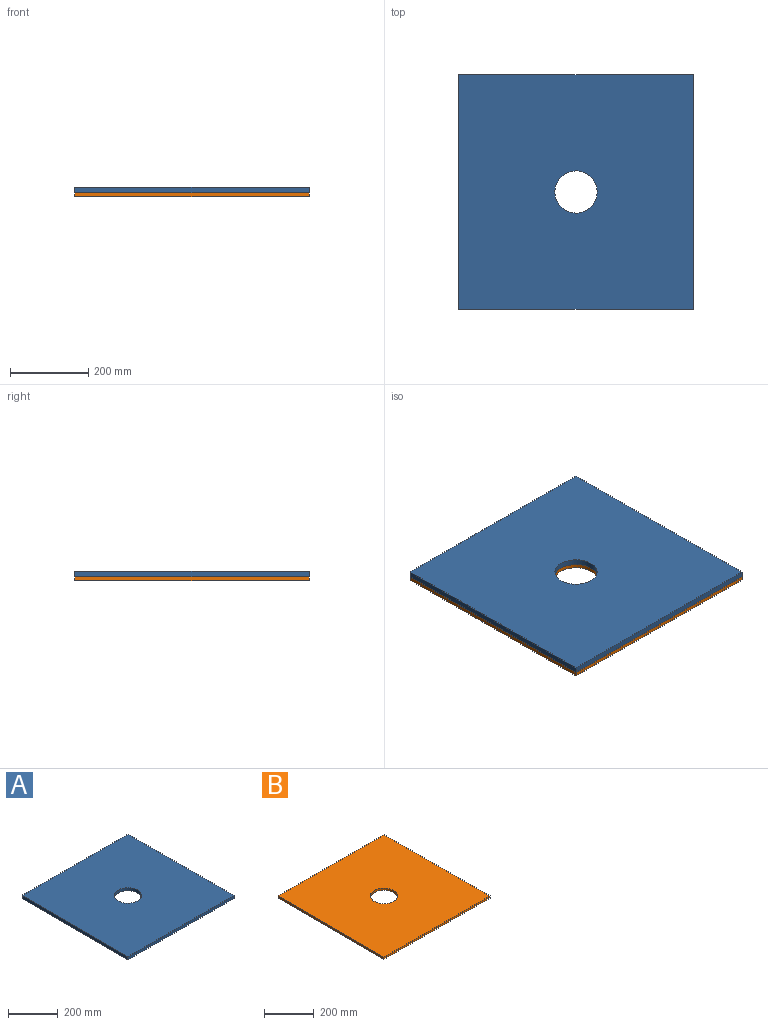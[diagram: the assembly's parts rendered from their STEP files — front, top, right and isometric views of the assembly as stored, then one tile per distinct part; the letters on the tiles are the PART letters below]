
ASSEMBLY  parts=2 mates=1
PART A: 7 faces, bbox 600x600x15 mm
  f0: plane 600x15mm, normal (-1,0,0), area 9000mm2, adj f1,f4,f5,f6
  f1: plane 600x15mm, normal (0,-1,0), area 9000mm2, adj f0,f2,f5,f6
  f2: plane 600x15mm, normal (1,0,0), area 9000mm2, adj f1,f4,f5,f6
  f3: cylinder r=53.98mm len=107.95mm, axis (0,0,-1), area 5087mm2, adj f5,f6
  f4: plane 600x15mm, normal (0,1,0), area 9000mm2, adj f0,f2,f5,f6
  f5: plane 600x600mm, normal (0,0,1), area 350847.6mm2, adj f0,f1,f2,f3,f4
  f6: plane 600x600mm, normal (0,0,-1), area 350847.6mm2, adj f0,f1,f2,f3,f4
PART B: 7 faces, bbox 600x600x10 mm
  f0: plane 600x10mm, normal (-1,0,0), area 6000mm2, adj f1,f4,f5,f6
  f1: plane 600x10mm, normal (0,-1,0), area 6000mm2, adj f0,f2,f5,f6
  f2: plane 600x10mm, normal (1,0,0), area 6000mm2, adj f1,f4,f5,f6
  f3: cylinder r=53.98mm len=107.95mm, axis (0,0,1), area 3391.3mm2, adj f5,f6
  f4: plane 600x10mm, normal (0,1,0), area 6000mm2, adj f0,f2,f5,f6
  f5: plane 600x600mm, normal (0,0,-1), area 350847.6mm2, adj f0,f1,f2,f3,f4
  f6: plane 600x600mm, normal (0,0,1), area 350847.6mm2, adj f0,f1,f2,f3,f4
PLACE A at identity
PLACE B at identity
MATE fastened A.f3 <-> B.f3  axis (0,0,-1) through (0,600,0)mm
